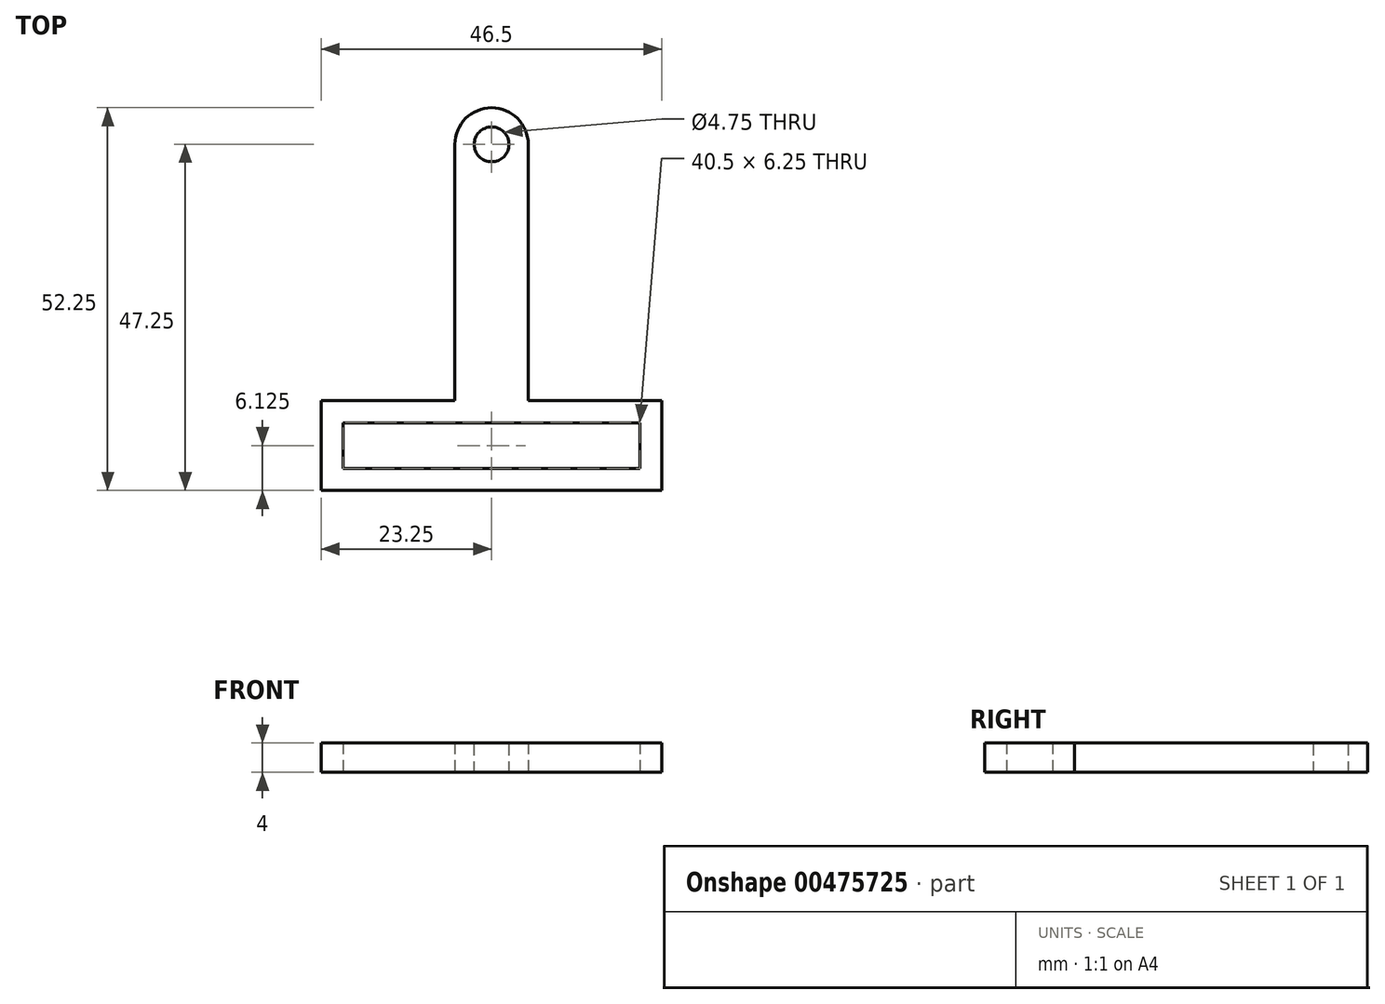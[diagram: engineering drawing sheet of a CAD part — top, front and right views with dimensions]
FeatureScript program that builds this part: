
annotation { "Feature Type Name" : "Feature", "Feature Type Description" : "" }
export const myFeature = defineFeature(function(context is Context, id is Id, definition is map)
    precondition{}
    {
        {
            var Q0;
            Q0=qCreatedBy(makeId("Top.planeOp"),FACE);
            var sketch = newSketch(context, id + "F0", { "sketchPlane" : qUnion([Q0])});
            skLineSegment(sketch, "E0.bottom", {"start": v(23.25, 0) * mm, "end": v(-23.25, 0) * mm});
            skLineSegment(sketch, "E0.top", {"start": v(23.25, -12.25) * mm, "end": v(-23.25, -12.25) * mm});
            skLineSegment(sketch, "E0.left", {"start": v(23.25, 0) * mm, "end": v(23.25, -12.25) * mm});
            skLineSegment(sketch, "E0.right", {"start": v(-23.25, 0) * mm, "end": v(-23.25, -12.25) * mm});
            skPoint(sketch, "E0.middle", {"position": v(0, -6.12) * mm});
            skLineSegment(sketch, "E1.bottom", {"start": v(20.25, -3) * mm, "end": v(-20.25, -3) * mm});
            skLineSegment(sketch, "E1.top", {"start": v(20.25, -9.25) * mm, "end": v(-20.25, -9.25) * mm});
            skLineSegment(sketch, "E1.left", {"start": v(20.25, -3) * mm, "end": v(20.25, -9.25) * mm});
            skLineSegment(sketch, "E1.right", {"start": v(-20.25, -3) * mm, "end": v(-20.25, -9.25) * mm});
            skLineSegment(sketch, "E2", {"start": v(20.25, 0) * mm, "end": v(20.25, -3) * mm});
            skLineSegment(sketch, "E3", {"start": v(20.25, -3) * mm, "end": v(23.25, -3) * mm});
            skLineSegment(sketch, "E4.bottom", {"start": v(5, 0) * mm, "end": v(-5, 0) * mm});
            skLineSegment(sketch, "E4.top", {"start": v(5, 40) * mm, "end": v(-5, 40) * mm});
            skLineSegment(sketch, "E4.left", {"start": v(5, 0) * mm, "end": v(5, 40) * mm});
            skLineSegment(sketch, "E4.right", {"start": v(-5, 0) * mm, "end": v(-5, 40) * mm});
            skPoint(sketch, "E4.middle", {"position": v(0, 20) * mm});
            skSolve(sketch);
        }
        {
            var Q0;
            Q0=qSketchRegion(id+"F0",true);
            extrude(context, id + "F1", {"entities" : qUnion([Q0]), "depth" : 4 * mm});
        }
        {
            var Q0;
            Q0=makeQuery(id+"F1.opExtrude","SWEPT_EDGE",EDGE,{"disambiguationData":[OSD([sQuery(id+"F0.wireOp",EDGE,"E4.top"),sQuery(id+"F0.wireOp",EDGE,"E4.left")])]});
            var Q1;
            Q1=makeQuery(id+"F1.opExtrude","SWEPT_EDGE",EDGE,{"disambiguationData":[OSD([sQuery(id+"F0.wireOp",EDGE,"E4.top"),sQuery(id+"F0.wireOp",EDGE,"E4.right")])]});
            fillet(context, id + "F2", {"entities" : qUnion([Q0, Q1]), "radius" : 5 * mm, "tangentPropagation" : true, "allowEdgeOverflow" : false});
        }
        {
            var Q0;
            Q0=makeQuery(id+"F1.opExtrude","CAP_FACE",FACE,{"disambiguationData":[OSD([sQuery(id+"F0.wireOp",EDGE,"E0.bottom"),sQuery(id+"F0.wireOp",EDGE,"E0.top"),sQuery(id+"F0.wireOp",EDGE,"E0.left"),sQuery(id+"F0.wireOp",EDGE,"E0.right"),sQuery(id+"F0.wireOp",EDGE,"E1.bottom"),sQuery(id+"F0.wireOp",EDGE,"E1.top"),sQuery(id+"F0.wireOp",EDGE,"E1.left"),sQuery(id+"F0.wireOp",EDGE,"E1.right"),sQuery(id+"F0.wireOp",EDGE,"E4.top"),sQuery(id+"F0.wireOp",EDGE,"E4.left"),sQuery(id+"F0.wireOp",EDGE,"E4.right")])],"isStart":false});
            var sketch = newSketch(context, id + "F3", { "sketchPlane" : qUnion([Q0])});
            skCircle(sketch, "E5", {"center": v(0, 35) * mm, "radius": 2.38 * mm});
            skSolve(sketch);
        }
        {
            var Q0;
            Q0=qSketchRegion(id+"F3",true);
            extrude(context, id + "F4", {"entities" : qUnion([Q0]), "operationType" : NewBodyOperationType.REMOVE, "endBound" : BoundingType.THROUGH_ALL, "oppositeDirection" : true, "depth" : 25 * mm});
        }
    });
